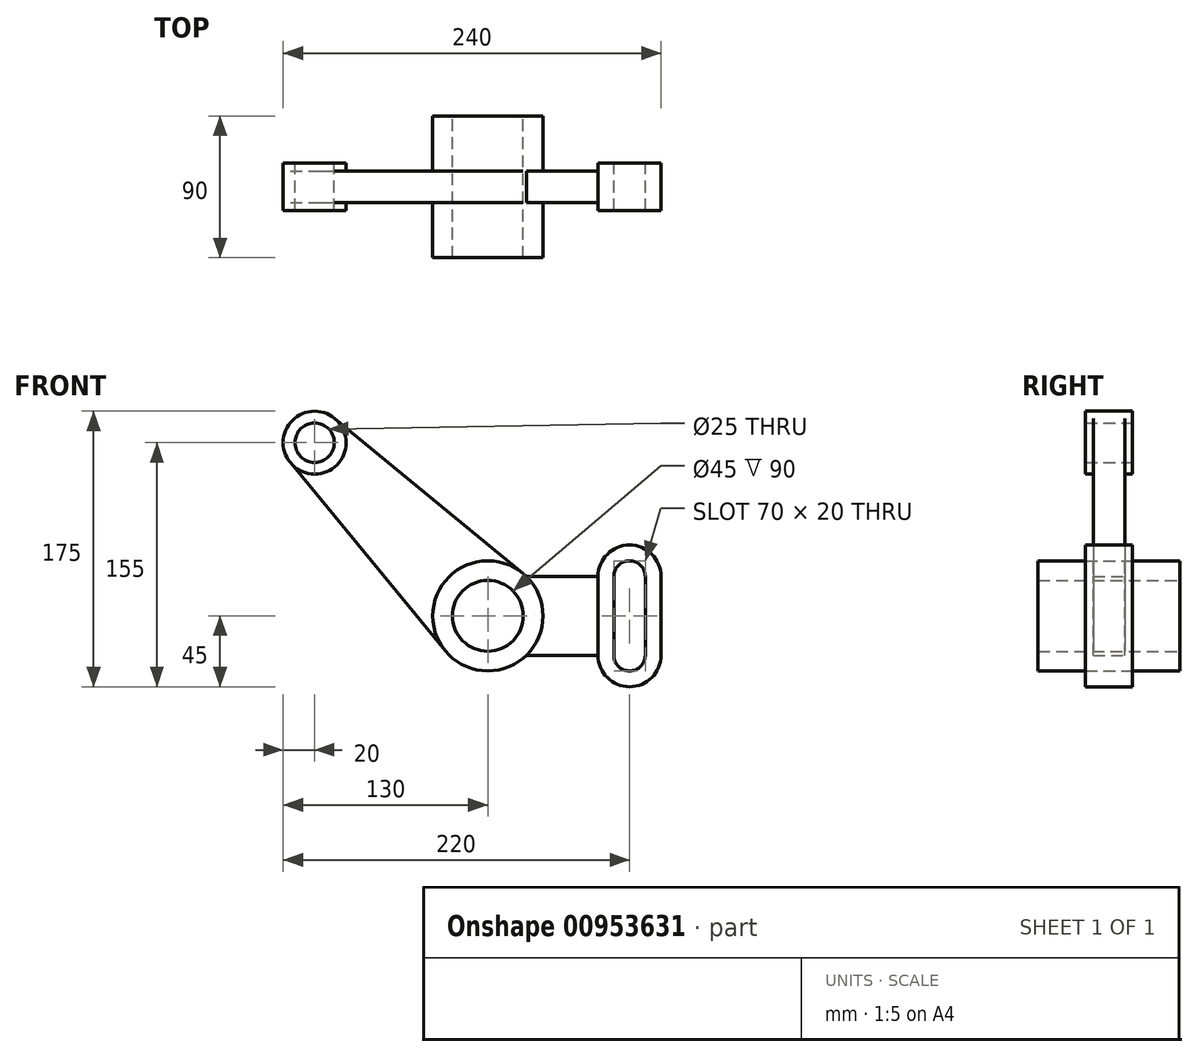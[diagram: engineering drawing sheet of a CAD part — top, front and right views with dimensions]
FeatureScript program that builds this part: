
annotation { "Feature Type Name" : "Feature", "Feature Type Description" : "" }
export const myFeature = defineFeature(function(context is Context, id is Id, definition is map)
    precondition{}
    {
        {
            var Q0;
            Q0=qCreatedBy(makeId("Front.planeOp"),FACE);
            var sketch = newSketch(context, id + "F0", { "sketchPlane" : qUnion([Q0])});
            skLineSegment(sketch, "E0", {"start": v(-98.1, 0) * mm, "end": v(117.82, 0) * mm, "construction": true});
            skLineSegment(sketch, "E1", {"start": v(0, 0) * mm, "end": v(-128.86, 128.86) * mm, "construction": true});
            skLineSegment(sketch, "E2", {"start": v(90, 90.18) * mm, "end": v(90, -33.06) * mm, "construction": true});
            skLineSegment(sketch, "E3", {"start": v(-110, 149.64) * mm, "end": v(-110, 19.36) * mm, "construction": true});
            skCircle(sketch, "E4", {"center": v(-110, 110) * mm, "radius": 12.5 * mm});
            skCircle(sketch, "E5", {"center": v(-110, 110) * mm, "radius": 20 * mm});
            skCircle(sketch, "E6", {"center": v(0, 0) * mm, "radius": 22.5 * mm});
            skCircle(sketch, "E7", {"center": v(0, 0) * mm, "radius": 35 * mm});
            skArc(sketch, "E8", {"start": v(110, 25) * mm, "mid": v(90, 45) * mm, "end": v(70, 25) * mm});
            skArc(sketch, "E9", {"start": v(100, 25) * mm, "mid": v(90, 35) * mm, "end": v(80, 25) * mm});
            skArc(sketch, "E10", {"start": v(70, -25) * mm, "mid": v(90, -45) * mm, "end": v(110, -25) * mm});
            skArc(sketch, "E11", {"start": v(80, -25) * mm, "mid": v(90, -35) * mm, "end": v(100, -25) * mm});
            skLineSegment(sketch, "E12", {"start": v(70, 25) * mm, "end": v(70, -25) * mm});
            skLineSegment(sketch, "E13", {"start": v(110, 25) * mm, "end": v(110, -25) * mm});
            skLineSegment(sketch, "E14", {"start": v(80, 25) * mm, "end": v(80, -25) * mm});
            skLineSegment(sketch, "E15", {"start": v(100, 25) * mm, "end": v(100, -25) * mm});
            skLineSegment(sketch, "E16", {"start": v(70, 25) * mm, "end": v(24.5, 25) * mm});
            skLineSegment(sketch, "E17", {"start": v(70, -25) * mm, "end": v(24.5, -25) * mm});
            skLineSegment(sketch, "E18", {"start": v(-97.29, 125.44) * mm, "end": v(24.7, 25) * mm});
            skLineSegment(sketch, "E19", {"start": v(-125.44, 97.29) * mm, "end": v(-27.02, -22.25) * mm});
            skPoint(sketch, "E20.orphan", {"position": v(0, -55.06) * mm});
            skSolve(sketch);
        }
        {
            var Q0;
            {var subQ3=sQuery(id+"F0.wireOp",EDGE,"E19");Q0=makeQuery(id+"F0.imprint","IMPRINT",FACE,{"disambiguationData":[TD([[makeQuery(id+"F0.imprint","IMPRINT",EDGE,{"derivedFrom":subQ3}),1.0]])]});}
            var Q1;
            {var subQ1=sQuery(id+"F0.wireOp",EDGE,"E12");Q1=makeQuery(id+"F0.imprint","IMPRINT",FACE,{"disambiguationData":[TD([[makeQuery(id+"F0.imprint","IMPRINT",EDGE,{"derivedFrom":subQ1}),-1.0]])]});}
            var Q2;
            Q2=makeQuery(id+"F0.imprint","IMPRINT",FACE,{"disambiguationData":[TD([[makeQuery(id+"F0.imprint","IMPRINT",EDGE,{"derivedFrom":sQuery(id+"F0.wireOp",EDGE,"E4")}),-1.0]])]});
            var Q3;
            Q3=makeQuery(id+"F0.imprint","IMPRINT",FACE,{"disambiguationData":[TD([[makeQuery(id+"F0.imprint","IMPRINT",EDGE,{"derivedFrom":sQuery(id+"F0.wireOp",EDGE,"E6")}),-1.0]])]});
            var Q4;
            Q4=makeQuery(id+"F0.imprint","IMPRINT",FACE,{"disambiguationData":[TD([[makeQuery(id+"F0.imprint","IMPRINT",EDGE,{"derivedFrom":sQuery(id+"F0.wireOp",EDGE,"E8")}),1.0]])]});
            extrude(context, id + "F1", {"entities" : qUnion([Q0, Q1, Q2, Q3, Q4]), "endBound" : BoundingType.SYMMETRIC, "depth" : 20 * mm, "offsetDistance" : 25 * mm});
        }
        {
            var Q0;
            Q0=makeQuery(id+"F0.imprint","IMPRINT",FACE,{"disambiguationData":[TD([[makeQuery(id+"F0.imprint","IMPRINT",EDGE,{"derivedFrom":sQuery(id+"F0.wireOp",EDGE,"E8")}),1.0]])]});
            var Q1;
            Q1=makeQuery(id+"F0.imprint","IMPRINT",FACE,{"disambiguationData":[TD([[makeQuery(id+"F0.imprint","IMPRINT",EDGE,{"derivedFrom":sQuery(id+"F0.wireOp",EDGE,"E4")}),-1.0]])]});
            extrude(context, id + "F2", {"entities" : qUnion([Q0, Q1]), "operationType" : NewBodyOperationType.ADD, "endBound" : BoundingType.SYMMETRIC, "depth" : 30 * mm, "offsetDistance" : 25 * mm});
        }
        {
            var Q0;
            Q0=makeQuery(id+"F0.imprint","IMPRINT",FACE,{"disambiguationData":[TD([[makeQuery(id+"F0.imprint","IMPRINT",EDGE,{"derivedFrom":sQuery(id+"F0.wireOp",EDGE,"E6")}),-1.0]])]});
            extrude(context, id + "F3", {"entities" : qUnion([Q0]), "operationType" : NewBodyOperationType.ADD, "endBound" : BoundingType.SYMMETRIC, "depth" : 90 * mm, "offsetDistance" : 25 * mm});
        }
    });
